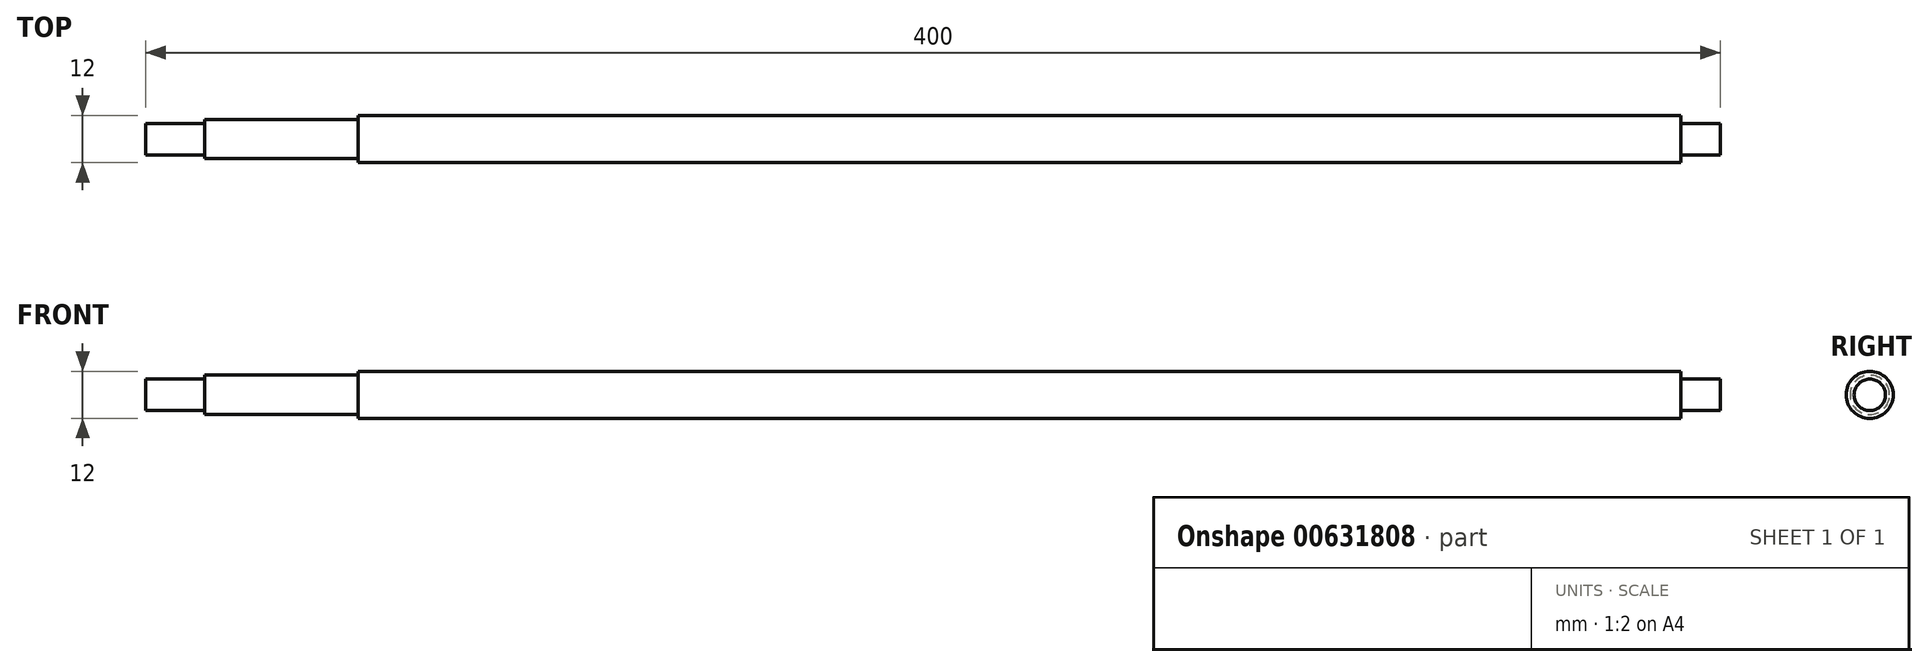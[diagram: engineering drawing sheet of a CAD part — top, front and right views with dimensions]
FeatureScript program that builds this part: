
annotation { "Feature Type Name" : "Feature", "Feature Type Description" : "" }
export const myFeature = defineFeature(function(context is Context, id is Id, definition is map)
    precondition{}
    {
        {
            var Q0;
            Q0=qCreatedBy(makeId("Right.planeOp"),FACE);
            var sketch = newSketch(context, id + "F0", { "sketchPlane" : qUnion([Q0])});
            skCircle(sketch, "E0", {"center": v(0, 0) * mm, "radius": 6 * mm});
            skSolve(sketch);
        }
        {
            var Q0;
            Q0=makeQuery(id+"F0.imprint","IMPRINT",FACE,{"disambiguationData":[TD([[makeQuery(id+"F0.imprint","IMPRINT",EDGE,{"derivedFrom":sQuery(id+"F0.wireOp",EDGE,"E0")}),1.0]])]});
            extrude(context, id + "F1", {"entities" : qUnion([Q0]), "endBound" : BoundingType.SYMMETRIC, "depth" : 400 * mm, "offsetDistance" : 25 * mm});
        }
        {
            var Q0;
            Q0=makeQuery(id+"F1.opExtrude","CAP_FACE",FACE,{"disambiguationData":[OSD([sQuery(id+"F0.wireOp",EDGE,"E0")])],"isStart":false});
            var sketch = newSketch(context, id + "F2", { "sketchPlane" : qUnion([Q0])});
            skCircle(sketch, "E1", {"center": v(0, 0) * mm, "radius": 4 * mm});
            skCircle(sketch, "E2", {"center": v(0, 0) * mm, "radius": 6 * mm});
            skSolve(sketch);
        }
        {
            var Q0;
            Q0 = qSketchRegion(id + "F2", true);
            extrude(context, id + "F3", {"entities" : qUnion([Q0]), "operationType" : NewBodyOperationType.REMOVE, "oppositeDirection" : true, "depth" : 10 * mm, "offsetDistance" : 25 * mm});
        }
        {
            var Q0;
            Q0=makeQuery(id+"F1.opExtrude","CAP_FACE",FACE,{"disambiguationData":[OSD([sQuery(id+"F0.wireOp",EDGE,"E0")])],"isStart":true});
            var sketch = newSketch(context, id + "F4", { "sketchPlane" : qUnion([Q0])});
            skCircle(sketch, "E3.0", {"center": v(0, 0) * mm, "radius": 6 * mm});
            skCircle(sketch, "E4", {"center": v(0, 0) * mm, "radius": 5 * mm});
            skSolve(sketch);
        }
        {
            var Q0;
            Q0=makeQuery(id+"F4.imprint","IMPRINT",FACE,{"disambiguationData":[TD([[makeQuery(id+"F4.imprint","IMPRINT",EDGE,{"derivedFrom":sQuery(id+"F4.wireOp",EDGE,"E3.0")}),-1.0]])]});
            extrude(context, id + "F5", {"entities" : qUnion([Q0]), "operationType" : NewBodyOperationType.REMOVE, "oppositeDirection" : true, "depth" : 54 * mm, "offsetDistance" : 25 * mm});
        }
        {
            var Q0;
            Q0=makeQuery(id+"F1.opExtrude","CAP_FACE",FACE,{"disambiguationData":[OSD([sQuery(id+"F0.wireOp",EDGE,"E0")])],"isStart":true});
            var sketch = newSketch(context, id + "F6", { "sketchPlane" : qUnion([Q0])});
            skCircle(sketch, "E5.0", {"center": v(0, 0) * mm, "radius": 5 * mm});
            skCircle(sketch, "E6", {"center": v(0, 0) * mm, "radius": 4 * mm});
            skSolve(sketch);
        }
        {
            var Q0;
            Q0 = qSketchRegion(id + "F6", true);
            extrude(context, id + "F7", {"entities" : qUnion([Q0]), "operationType" : NewBodyOperationType.REMOVE, "oppositeDirection" : true, "depth" : 15 * mm, "offsetDistance" : 25 * mm});
        }
    });
